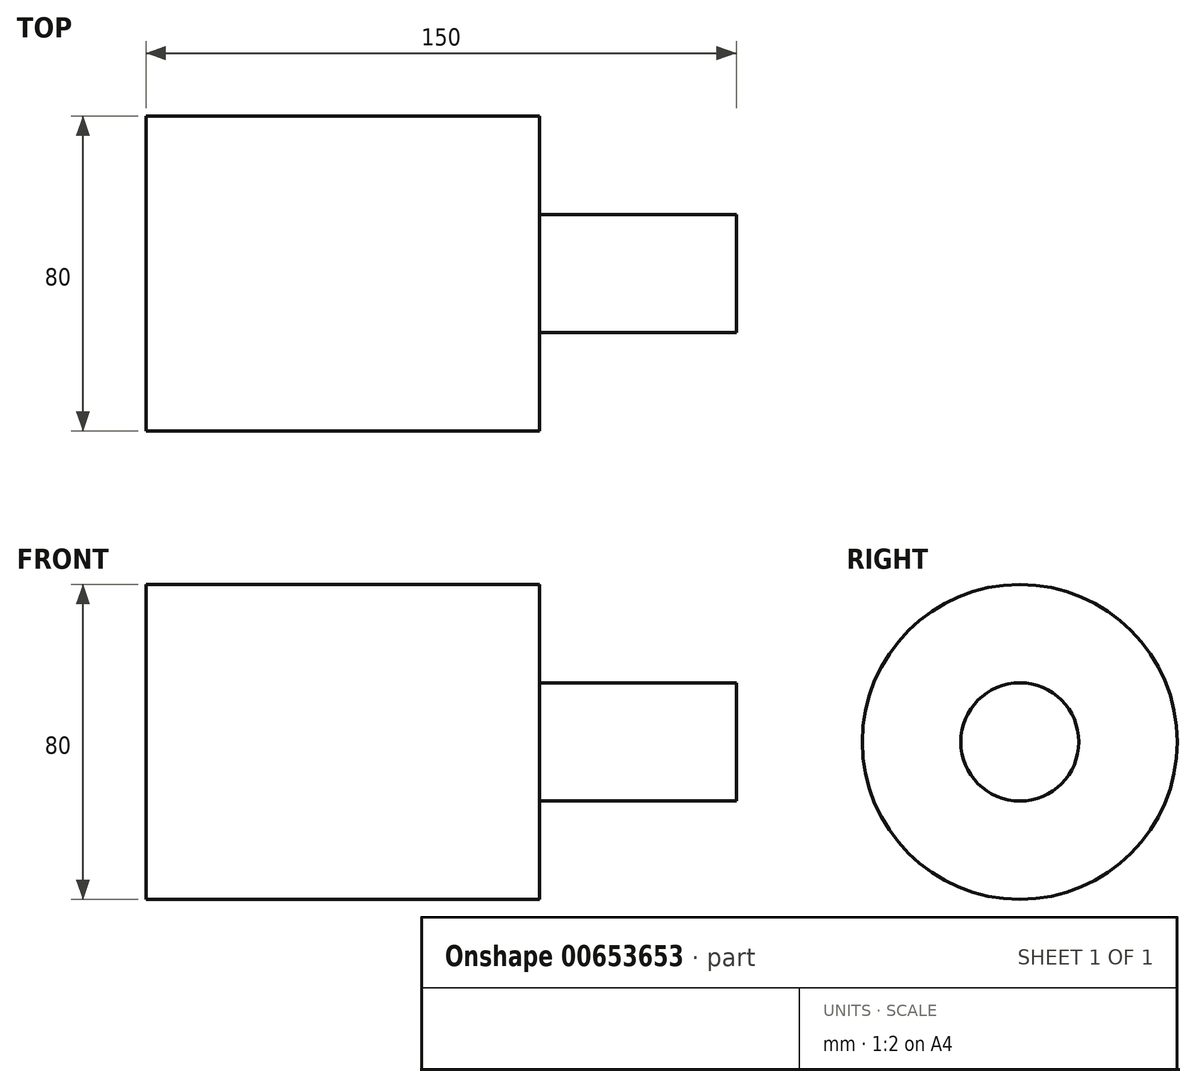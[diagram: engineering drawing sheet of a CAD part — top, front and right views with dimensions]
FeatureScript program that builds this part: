
annotation { "Feature Type Name" : "Feature", "Feature Type Description" : "" }
export const myFeature = defineFeature(function(context is Context, id is Id, definition is map)
    precondition{}
    {
        {
            var Q0;
            Q0=qCreatedBy(makeId("Right.planeOp"),FACE);
            var sketch = newSketch(context, id + "F0", { "sketchPlane" : qUnion([Q0])});
            skCircle(sketch, "E0", {"center": v(0, 0) * mm, "radius": 40 * mm});
            skSolve(sketch);
        }
        {
            var Q0;
            Q0 = qSketchRegion(id + "F0", true);
            extrude(context, id + "F1", {"entities" : qUnion([Q0]), "depth" : 100 * mm, "offsetDistance" : 25 * mm});
        }
        {
            var Q0;
            Q0=makeQuery(id+"F1.opExtrude","CAP_FACE",FACE,{"disambiguationData":[OSD([sQuery(id+"F0.wireOp",EDGE,"E0")])],"isStart":false});
            var sketch = newSketch(context, id + "F2", { "sketchPlane" : qUnion([Q0])});
            skCircle(sketch, "E1", {"center": v(0, 0) * mm, "radius": 15 * mm});
            skSolve(sketch);
        }
        {
            var Q0;
            Q0=makeQuery(id+"F2.imprint","IMPRINT",FACE,{"disambiguationData":[TD([[makeQuery(id+"F2.imprint","IMPRINT",EDGE,{"derivedFrom":sQuery(id+"F2.wireOp",EDGE,"E1")}),1.0]])]});
            extrude(context, id + "F3", {"entities" : qUnion([Q0]), "operationType" : NewBodyOperationType.ADD, "depth" : 50 * mm, "offsetDistance" : 25 * mm});
        }
    });
